# Revit family: hansgrohe_56053XXX-RainDrain-Flex-Linear-shower-dr
name_source: partatom
category: Generic Models
revit_build: Autodesk Revit 2018 (Build: 20170223_1515(x64)
units: mm (PartAtom-declared; Revit-internal decimal feet)

## family parameters
Always vertical = No
Can host rebar = No
Cut with Voids When Loaded = No
Part Type = Normal
Room Calculation Point = No
Round Connector Dimension = Use Diameter
Shared = No
Work Plane-Based = No

## types (1)
- Default
    Brand url = http://www.hansgrohe-int.com
    Design country = Germany
    Edition number = 1
    GTIN code = https://4059625349601
    IFC Classification = Sanitary Terminal
    Installation instructions = https://www.hansgrohe.com
    Manufacturer country = Germany
    Manufacturer name = hansgrohe
    Material = Hansgrohe - Paket Wright - 990 Polished Gold Optic
    Material main = Stainless steel
    Product Guid = bbae56fd-a943-4f1d-bb13-506d1c05dad6
    Product SKU = 56053XXX
    Product data url = https://bimobject.com
    Product family = RainDrain Flex
    Product group = Shower drains
    Product name = 56053XXX RainDrain Flex Linear shower drain 100 cm cuttable for wall mounting
    Product url = https://www.hansgrohe.com
    QR code = http://bimobject.com
    Technical description = https://www.hansgrohe.com

## geometry (parser evidence)
native form markers: Sweep x3
no freeform markers — native parametric forms only
